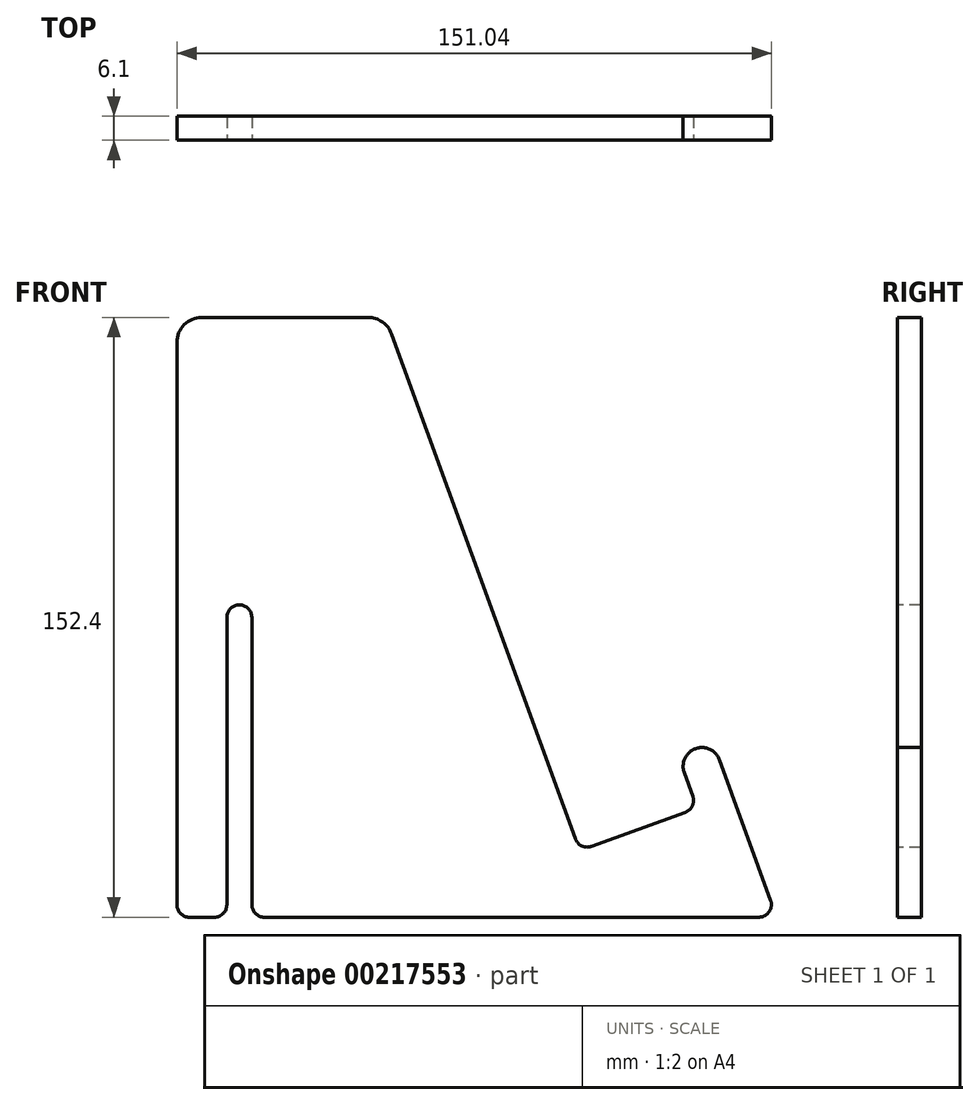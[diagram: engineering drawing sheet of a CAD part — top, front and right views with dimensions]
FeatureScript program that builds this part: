
annotation { "Feature Type Name" : "Feature", "Feature Type Description" : "" }
export const myFeature = defineFeature(function(context is Context, id is Id, definition is map)
    precondition{}
    {
        {
            var Q0;
            Q0=qCreatedBy(makeId("Front.planeOp"),FACE);
            var sketch = newSketch(context, id + "F0", { "sketchPlane" : qUnion([Q0])});
            skLineSegment(sketch, "E0", {"start": v(-146.05, 152.4) * mm, "end": v(-103.84, 152.4) * mm});
            skLineSegment(sketch, "E1", {"start": v(-97.87, 148.22) * mm, "end": v(-51.16, 19.9) * mm});
            skLineSegment(sketch, "E2", {"start": v(-47.1, 18) * mm, "end": v(-23.23, 26.68) * mm});
            skLineSegment(sketch, "E3", {"start": v(-152.4, 146.05) * mm, "end": v(-152.4, 3.17) * mm});
            skLineSegment(sketch, "E4", {"start": v(-149.22, 0) * mm, "end": v(-142.87, 0) * mm});
            skLineSegment(sketch, "E5", {"start": v(-139.7, 3.18) * mm, "end": v(-139.7, 76.2) * mm});
            skLineSegment(sketch, "E6", {"start": v(-136.52, 79.37) * mm, "end": v(-136.53, 79.37) * mm});
            skLineSegment(sketch, "E7", {"start": v(-133.35, 76.2) * mm, "end": v(-133.35, 3.18) * mm});
            skLineSegment(sketch, "E8", {"start": v(-130.17, 0) * mm, "end": v(-4.53, 0) * mm});
            skLineSegment(sketch, "E9", {"start": v(-21.33, 30.75) * mm, "end": v(-23.5, 36.72) * mm});
            skPoint(sketch, "E10.visualSharp", {"position": v(-26.14, 43.96) * mm});
            skPoint(sketch, "E11.visualSharp", {"position": v(0, 44.45) * mm});
            skPoint(sketch, "E12.visualSharp", {"position": v(0, 0) * mm});
            skPoint(sketch, "E13.visualSharp", {"position": v(-133.35, 0) * mm});
            skArc(sketch, "E13.filletArc", {"start": v(-133.35, 3.17) * mm, "mid": v(-132.42, 0.93) * mm, "end": v(-130.17, 0) * mm});
            skPoint(sketch, "E14.visualSharp", {"position": v(-139.7, 0) * mm});
            skArc(sketch, "E14.filletArc", {"start": v(-142.87, 0) * mm, "mid": v(-140.63, 0.93) * mm, "end": v(-139.7, 3.18) * mm});
            skPoint(sketch, "E15.visualSharp", {"position": v(-139.7, 79.37) * mm});
            skArc(sketch, "E15.filletArc", {"start": v(-136.52, 79.37) * mm, "mid": v(-138.77, 78.45) * mm, "end": v(-139.7, 76.2) * mm});
            skPoint(sketch, "E16.visualSharp", {"position": v(-133.35, 79.37) * mm});
            skArc(sketch, "E16.filletArc", {"start": v(-133.35, 76.2) * mm, "mid": v(-134.28, 78.45) * mm, "end": v(-136.53, 79.37) * mm});
            skPoint(sketch, "E17.visualSharp", {"position": v(-152.4, 0) * mm});
            skArc(sketch, "E17.filletArc", {"start": v(-152.4, 3.17) * mm, "mid": v(-151.47, 0.93) * mm, "end": v(-149.22, 0) * mm});
            skPoint(sketch, "E18.visualSharp", {"position": v(-152.4, 152.4) * mm});
            skArc(sketch, "E18.filletArc", {"start": v(-146.05, 152.4) * mm, "mid": v(-150.54, 150.54) * mm, "end": v(-152.4, 146.05) * mm});
            skPoint(sketch, "E19.visualSharp", {"position": v(-99.4, 152.4) * mm});
            skArc(sketch, "E19.filletArc", {"start": v(-97.87, 148.22) * mm, "mid": v(-100.2, 151.25) * mm, "end": v(-103.84, 152.4) * mm});
            skPoint(sketch, "E20.visualSharp", {"position": v(-50.08, 16.9) * mm});
            skArc(sketch, "E20.filletArc", {"start": v(-51.16, 19.9) * mm, "mid": v(-49.52, 18.1) * mm, "end": v(-47.1, 18) * mm});
            skPoint(sketch, "E21.visualSharp", {"position": v(-20.24, 27.77) * mm});
            skArc(sketch, "E21.filletArc", {"start": v(-23.23, 26.68) * mm, "mid": v(-21.44, 28.32) * mm, "end": v(-21.33, 30.75) * mm});
            skLineSegment(sketch, "E22.0", {"start": v(-1.55, 4.26) * mm, "end": v(-14.55, 39.98) * mm});
            skArc(sketch, "E23.filletArc", {"start": v(-4.53, 0) * mm, "mid": v(-1.93, 1.35) * mm, "end": v(-1.55, 4.26) * mm});
            skArc(sketch, "E24", {"start": v(-14.55, 39.98) * mm, "mid": v(-20.65, 42.82) * mm, "end": v(-23.5, 36.72) * mm});
            skSolve(sketch);
        }
        {
            var Q0;
            Q0=makeQuery(id+"F0.imprint","IMPRINT",FACE,{"disambiguationData":[TD([[makeQuery(id+"F0.imprint","IMPRINT",EDGE,{"derivedFrom":sQuery(id+"F0.wireOp",EDGE,"E0")}),-1.0]])]});
            extrude(context, id + "F1", {"entities" : qUnion([Q0]), "oppositeDirection" : true, "depth" : 6.1 * mm});
        }
    });
